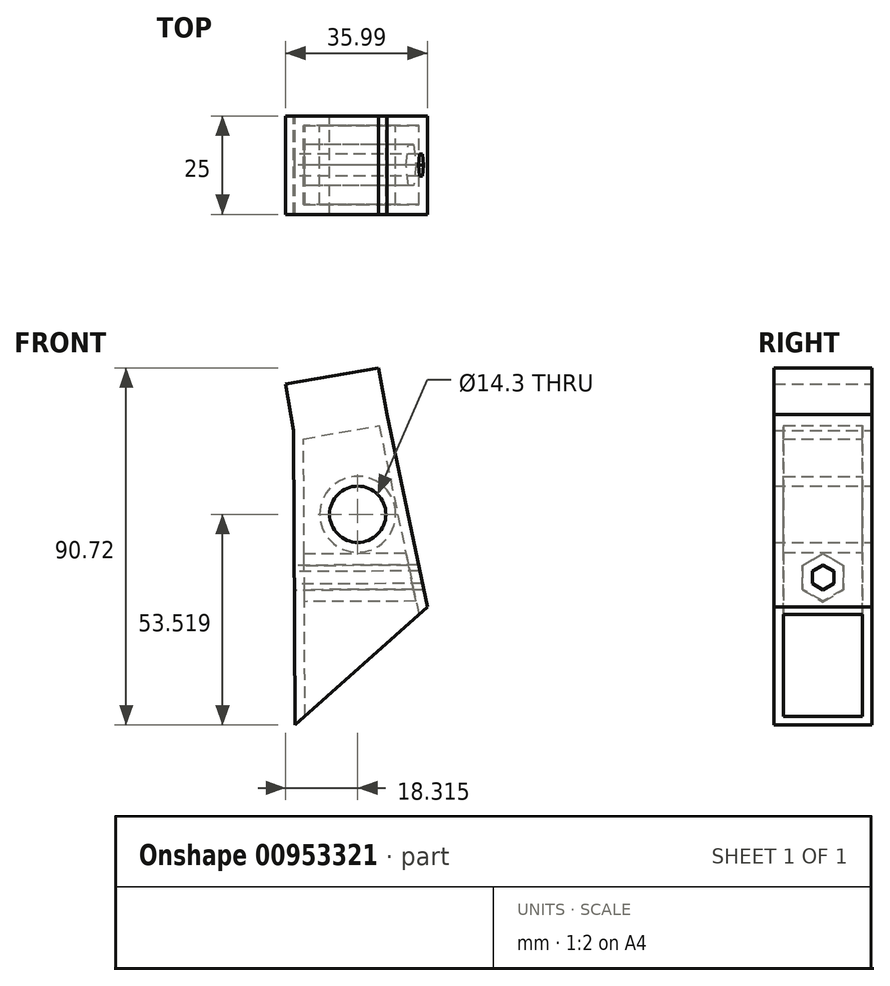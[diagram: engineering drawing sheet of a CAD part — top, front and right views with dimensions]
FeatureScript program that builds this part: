
annotation { "Feature Type Name" : "Feature", "Feature Type Description" : "" }
export const myFeature = defineFeature(function(context is Context, id is Id, definition is map)
    precondition{}
    {
        {
            var Q0;
            Q0=qCreatedBy(makeId("Front.planeOp"),FACE);
            var sketch = newSketch(context, id + "F0", { "sketchPlane" : qUnion([Q0])});
            skLineSegment(sketch, "E0", {"start": v(-38.7, 0) * mm, "end": v(-15.06, 4.1) * mm});
            skLineSegment(sketch, "E1", {"start": v(-15.06, 4.1) * mm, "end": v(-4.76, -44.84) * mm});
            skLineSegment(sketch, "E2", {"start": v(-4.76, -44.84) * mm, "end": v(-38.33, -74.81) * mm});
            skLineSegment(sketch, "E3", {"start": v(-38.33, -74.81) * mm, "end": v(-38.7, 0.19) * mm});
            skSolve(sketch);
        }
        {
            var Q0;
            Q0=qCreatedBy(makeId("Front.planeOp"),FACE);
            var sketch = newSketch(context, id + "F1", { "sketchPlane" : qUnion([Q0])});
            skCircle(sketch, "E4", {"center": v(-22.44, -21.3) * mm, "radius": 7.15 * mm});
            skSolve(sketch);
        }
        {
            var Q0;
            Q0 = qSketchRegion(id + "F0", true);
            extrude(context, id + "F2", {"entities" : qUnion([Q0]), "depth" : 25 * mm, "offsetDistance" : 25 * mm});
        }
        {
            var Q0;
            Q0 = qSketchRegion(id + "F1", true);
            extrude(context, id + "F3", {"entities" : qUnion([Q0]), "operationType" : NewBodyOperationType.REMOVE, "depth" : 25.4 * mm, "offsetDistance" : 25 * mm});
        }
        {
            var Q0;
            Q0=makeQuery(id+"F2.opExtrude","SWEPT_FACE",FACE,{"disambiguationData":[OSD([sQuery(id+"F0.wireOp",EDGE,"E3")])]});
            var sketch = newSketch(context, id + "F4", { "sketchPlane" : qUnion([Q0])});
            skLineSegment(sketch, "E5", {"start": v(25, 0.2) * mm, "end": v(25, -74.62) * mm});
            skCircle(sketch, "E6.cCircle", {"center": v(12.48, -37.26) * mm, "radius": 2.75 * mm, "construction": true});
            skLineSegment(sketch, "E6.0", {"start": v(15.23, -35.67) * mm, "end": v(15.23, -38.85) * mm});
            skLineSegment(sketch, "E6.1", {"start": v(15.23, -38.85) * mm, "end": v(12.48, -40.44) * mm});
            skLineSegment(sketch, "E6.2", {"start": v(12.48, -40.44) * mm, "end": v(9.73, -38.85) * mm});
            skLineSegment(sketch, "E6.3", {"start": v(9.73, -38.85) * mm, "end": v(9.73, -35.67) * mm});
            skLineSegment(sketch, "E6.4", {"start": v(9.73, -35.67) * mm, "end": v(12.48, -34.08) * mm});
            skLineSegment(sketch, "E6.5", {"start": v(12.48, -34.08) * mm, "end": v(15.23, -35.67) * mm});
            skPoint(sketch, "E6.0.midPoint", {"position": v(15.23, -37.26) * mm});
            skSolve(sketch);
        }
        {
            var Q0;
            {var subQ0=sQuery(id+"F0.wireOp",EDGE,"E3");Q0=makeQuery(id+"F4.imprint","IMPRINT",FACE,{"disambiguationData":[TD([[makeQuery(id+"F4.imprint","IMPRINT",EDGE,{"derivedFrom":makeQuery(id+"F2.opExtrude","CAP_EDGE",EDGE,{"disambiguationData":[OSD([subQ0])],"isStart":true})}),-1.0]])]});}
            var sketch = newSketch(context, id + "F5", { "sketchPlane" : qUnion([Q0])});
            skSolve(sketch);
        }
        {
            var Q0;
            Q0=makeQuery(id+"F5.imprint","IMPRINT",FACE,{"disambiguationData":[TD([[makeQuery(id+"F5.imprint","IMPRINT",EDGE,{"derivedFrom":makeQuery(id+"F4.imprint","IMPRINT",EDGE,{"derivedFrom":sQuery(id+"F4.wireOp",EDGE,"E6.0")})}),-1.0]])]});
            extrude(context, id + "F6", {"entities" : qUnion([Q0]), "operationType" : NewBodyOperationType.REMOVE, "endBound" : BoundingType.SYMMETRIC, "oppositeDirection" : true, "depth" : 70.4 * mm, "offsetDistance" : 25 * mm});
        }
        {
            var Q0;
            Q0=makeQuery(id+"F2.opExtrude","SWEPT_FACE",FACE,{"disambiguationData":[OSD([sQuery(id+"F0.wireOp",EDGE,"E2")])]});
            shell(context, id + "F7", {"entities" : qUnion([Q0]), "thickness" : 2.5 * mm});
        }
        {
            var Q0;
            Q0=makeQuery(id+"F2.opExtrude","SWEPT_FACE",FACE,{"disambiguationData":[OSD([sQuery(id+"F0.wireOp",EDGE,"E0")])]});
            extrude(context, id + "F8", {"entities" : qUnion([Q0]), "operationType" : NewBodyOperationType.ADD, "depth" : 12 * mm, "offsetDistance" : 25 * mm});
        }
    });
